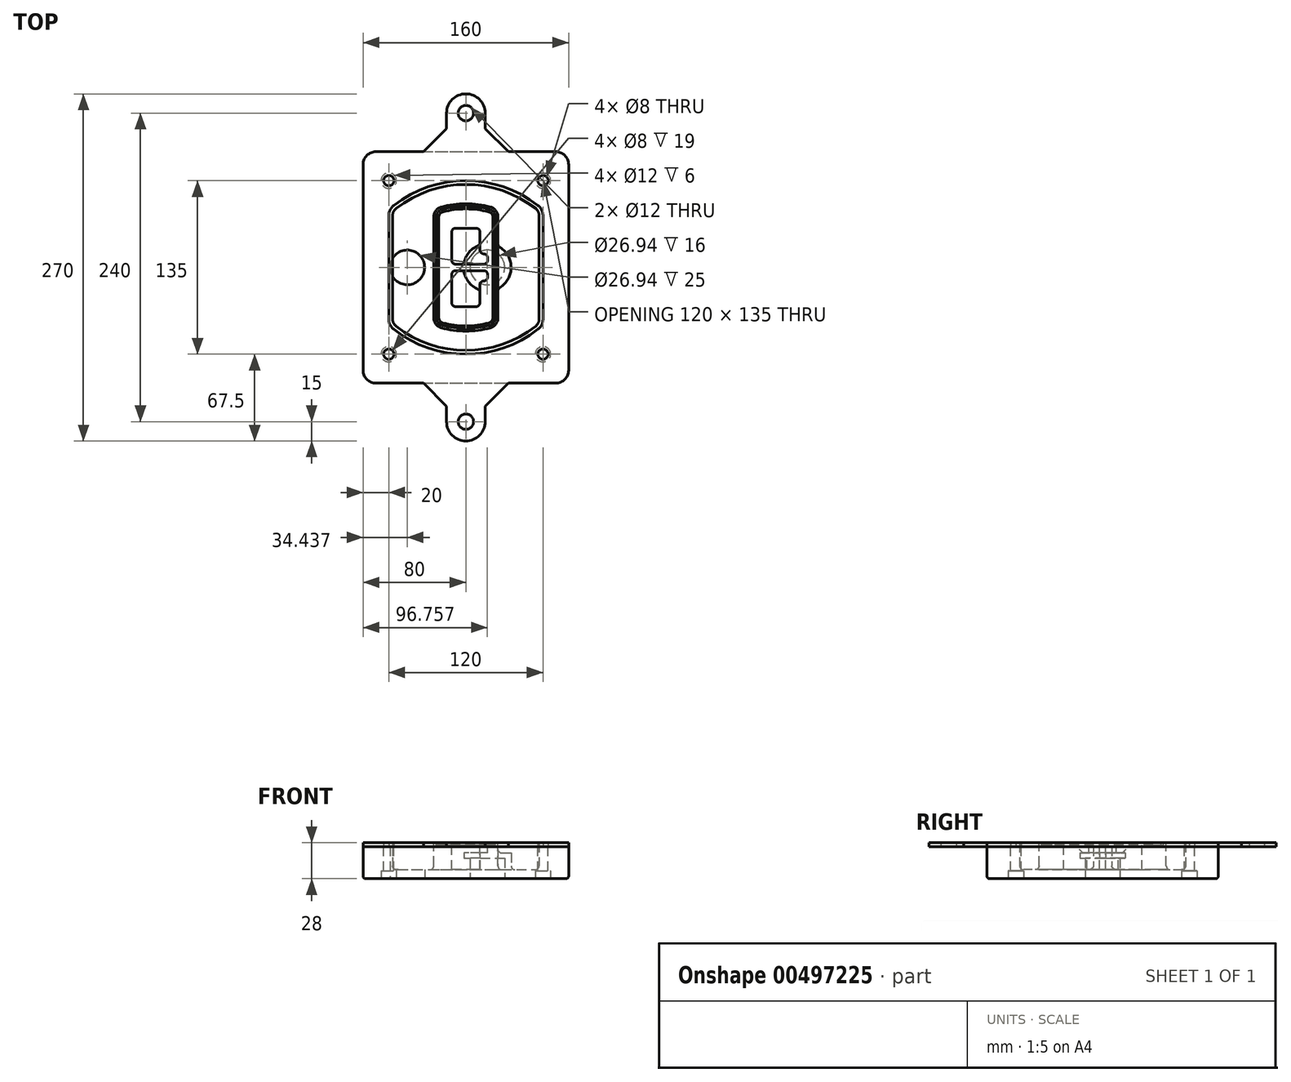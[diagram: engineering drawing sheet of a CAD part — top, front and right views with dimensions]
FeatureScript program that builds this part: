
annotation { "Feature Type Name" : "Feature", "Feature Type Description" : "" }
export const myFeature = defineFeature(function(context is Context, id is Id, definition is map)
    precondition{}
    {
        {
            var Q0;
            Q0=qCreatedBy(makeId("Top.planeOp"),FACE);
            var sketch = newSketch(context, id + "F0", { "sketchPlane" : qUnion([Q0])});
            skPoint(sketch, "E0.rect.middle", {"position": v(0, 0) * mm});
            skLineSegment(sketch, "E1.bottom", {"start": v(-70, -90) * mm, "end": v(70, -90) * mm});
            skLineSegment(sketch, "E1.top", {"start": v(-70, 90) * mm, "end": v(70, 90) * mm});
            skLineSegment(sketch, "E1.left", {"start": v(-80, -80) * mm, "end": v(-80, 80) * mm});
            skLineSegment(sketch, "E1.right", {"start": v(80, -80) * mm, "end": v(80, 80) * mm});
            skLineSegment(sketch, "E2", {"start": v(-80, 90) * mm, "end": v(80, -90) * mm, "construction": true});
            skLineSegment(sketch, "E3", {"start": v(80, 90) * mm, "end": v(-80, -90) * mm, "construction": true});
            skCircle(sketch, "E4", {"center": v(-60, 67.5) * mm, "radius": 4 * mm});
            skCircle(sketch, "E5", {"center": v(60, 67.5) * mm, "radius": 4 * mm});
            skCircle(sketch, "E6", {"center": v(60, -67.5) * mm, "radius": 4 * mm});
            skCircle(sketch, "E7", {"center": v(-60, -67.5) * mm, "radius": 4 * mm});
            skLineSegment(sketch, "E8", {"start": v(-60, 67.5) * mm, "end": v(60, 67.5) * mm, "construction": true});
            skLineSegment(sketch, "E9", {"start": v(60, 67.5) * mm, "end": v(60, -67.5) * mm, "construction": true});
            skLineSegment(sketch, "E10", {"start": v(60, -67.5) * mm, "end": v(-60, -67.5) * mm, "construction": true});
            skLineSegment(sketch, "E11", {"start": v(-60, -67.5) * mm, "end": v(-60, 67.5) * mm, "construction": true});
            skLineSegment(sketch, "E12", {"start": v(-60, 40.3) * mm, "end": v(-60, -40.3) * mm});
            skLineSegment(sketch, "E13", {"start": v(60, 40.3) * mm, "end": v(60, -40.3) * mm});
            skArc(sketch, "E14", {"start": v(56.15, 48.18) * mm, "mid": v(0, 67.5) * mm, "end": v(-56.15, 48.18) * mm});
            skArc(sketch, "E15", {"start": v(-56.15, -48.18) * mm, "mid": v(0, -67.5) * mm, "end": v(56.15, -48.18) * mm});
            skLineSegment(sketch, "E16", {"start": v(-60, 0) * mm, "end": v(60, 0) * mm, "construction": true});
            skPoint(sketch, "E17.visualSharp", {"position": v(-60, -45) * mm});
            skArc(sketch, "E17.filletArc", {"start": v(-60, -40.3) * mm, "mid": v(-58.99, -44.68) * mm, "end": v(-56.15, -48.18) * mm});
            skPoint(sketch, "E18.visualSharp", {"position": v(-60, 45) * mm});
            skArc(sketch, "E18.filletArc", {"start": v(-56.15, 48.18) * mm, "mid": v(-58.99, 44.68) * mm, "end": v(-60, 40.3) * mm});
            skPoint(sketch, "E19.visualSharp", {"position": v(60, 45) * mm});
            skArc(sketch, "E19.filletArc", {"start": v(60, 40.3) * mm, "mid": v(58.99, 44.68) * mm, "end": v(56.15, 48.18) * mm});
            skPoint(sketch, "E20.visualSharp", {"position": v(60, -45) * mm});
            skArc(sketch, "E20.filletArc", {"start": v(56.15, -48.18) * mm, "mid": v(58.99, -44.68) * mm, "end": v(60, -40.3) * mm});
            skPoint(sketch, "E21.visualSharp", {"position": v(-80, 90) * mm});
            skArc(sketch, "E21.filletArc", {"start": v(-70, 90) * mm, "mid": v(-77.07, 87.07) * mm, "end": v(-80, 80) * mm});
            skPoint(sketch, "E22.visualSharp", {"position": v(80, 90) * mm});
            skArc(sketch, "E22.filletArc", {"start": v(80, 80) * mm, "mid": v(77.07, 87.07) * mm, "end": v(70, 90) * mm});
            skPoint(sketch, "E23.visualSharp", {"position": v(80, -90) * mm});
            skArc(sketch, "E23.filletArc", {"start": v(70, -90) * mm, "mid": v(77.07, -87.07) * mm, "end": v(80, -80) * mm});
            skPoint(sketch, "E24.visualSharp", {"position": v(-80, -90) * mm});
            skArc(sketch, "E24.filletArc", {"start": v(-80, -80) * mm, "mid": v(-77.07, -87.07) * mm, "end": v(-70, -90) * mm});
            skArc(sketch, "E25.0", {"start": v(57, 40.3) * mm, "mid": v(56.3, 43.36) * mm, "end": v(54.3, 45.81) * mm});
            skLineSegment(sketch, "E25.1", {"start": v(57, 40.3) * mm, "end": v(57, -40.3) * mm});
            skArc(sketch, "E25.2", {"start": v(54.3, -45.81) * mm, "mid": v(56.3, -43.36) * mm, "end": v(57, -40.3) * mm});
            skArc(sketch, "E25.3", {"start": v(-54.3, -45.81) * mm, "mid": v(0, -64.5) * mm, "end": v(54.3, -45.81) * mm});
            skArc(sketch, "E25.4", {"start": v(-57, -40.3) * mm, "mid": v(-56.3, -43.36) * mm, "end": v(-54.3, -45.81) * mm});
            skArc(sketch, "E25.5", {"start": v(54.3, 45.81) * mm, "mid": v(0, 64.5) * mm, "end": v(-54.3, 45.81) * mm});
            skLineSegment(sketch, "E25.6", {"start": v(-57, 40.3) * mm, "end": v(-57, -40.3) * mm});
            skArc(sketch, "E25.7", {"start": v(-54.3, 45.81) * mm, "mid": v(-56.3, 43.36) * mm, "end": v(-57, 40.3) * mm});
            skArc(sketch, "E26.0", {"start": v(-58.62, 51.33) * mm, "mid": v(-62.58, 46.43) * mm, "end": v(-64, 40.3) * mm});
            skArc(sketch, "E26.1", {"start": v(58.62, 51.33) * mm, "mid": v(0, 71.5) * mm, "end": v(-58.62, 51.33) * mm});
            skArc(sketch, "E26.2", {"start": v(64, 40.3) * mm, "mid": v(62.58, 46.43) * mm, "end": v(58.62, 51.33) * mm});
            skLineSegment(sketch, "E26.3", {"start": v(64, 40.3) * mm, "end": v(64, -40.3) * mm});
            skArc(sketch, "E26.4", {"start": v(58.62, -51.33) * mm, "mid": v(62.58, -46.43) * mm, "end": v(64, -40.3) * mm});
            skLineSegment(sketch, "E26.5", {"start": v(-64, 40.3) * mm, "end": v(-64, -40.3) * mm});
            skArc(sketch, "E26.6", {"start": v(-58.62, -51.33) * mm, "mid": v(0, -71.5) * mm, "end": v(58.62, -51.33) * mm});
            skArc(sketch, "E26.7", {"start": v(-64, -40.3) * mm, "mid": v(-62.58, -46.43) * mm, "end": v(-58.62, -51.33) * mm});
            skSolve(sketch);
        }
        {
            var Q0;
            Q0=makeQuery(id+"F0.imprint","IMPRINT",FACE,{"disambiguationData":[TD([[makeQuery(id+"F0.imprint","IMPRINT",EDGE,{"derivedFrom":sQuery(id+"F0.wireOp",EDGE,"E1.bottom")}),1.0]])]});
            var Q1;
            Q1=makeQuery(id+"F0.imprint","IMPRINT",FACE,{"disambiguationData":[TD([[makeQuery(id+"F0.imprint","IMPRINT",EDGE,{"derivedFrom":sQuery(id+"F0.wireOp",EDGE,"E12")}),1.0]])]});
            var Q2;
            Q2=makeQuery(id+"F0.imprint","IMPRINT",FACE,{"disambiguationData":[TD([[makeQuery(id+"F0.imprint","IMPRINT",EDGE,{"derivedFrom":sQuery(id+"F0.wireOp",EDGE,"E25.0")}),1.0]])]});
            var Q3;
            Q3=makeQuery(id+"F0.imprint","IMPRINT",FACE,{"disambiguationData":[TD([[makeQuery(id+"F0.imprint","IMPRINT",EDGE,{"derivedFrom":sQuery(id+"F0.wireOp",EDGE,"E12")}),-1.0]])]});
            extrude(context, id + "F1", {"entities" : qUnion([Q0, Q1, Q2, Q3]), "oppositeDirection" : true, "depth" : 25 * mm});
        }
        {
            var Q0;
            Q0=makeQuery(id+"F0.imprint","IMPRINT",FACE,{"disambiguationData":[TD([[makeQuery(id+"F0.imprint","IMPRINT",EDGE,{"derivedFrom":sQuery(id+"F0.wireOp",EDGE,"E12")}),1.0]])]});
            extrude(context, id + "F2", {"entities" : qUnion([Q0]), "operationType" : NewBodyOperationType.ADD, "depth" : 3 * mm});
        }
        {
            var Q0;
            Q0=makeQuery(id+"F0.imprint","IMPRINT",FACE,{"disambiguationData":[TD([[makeQuery(id+"F0.imprint","IMPRINT",EDGE,{"derivedFrom":sQuery(id+"F0.wireOp",EDGE,"E25.0")}),1.0]])]});
            extrude(context, id + "F3", {"entities" : qUnion([Q0]), "operationType" : NewBodyOperationType.REMOVE, "oppositeDirection" : true, "depth" : 18 * mm});
        }
        {
            var Q0;
            Q0=makeQuery(id+"F2.opExtrude","CAP_FACE",FACE,{"disambiguationData":[OSD([sQuery(id+"F0.wireOp",EDGE,"E12"),sQuery(id+"F0.wireOp",EDGE,"E13"),sQuery(id+"F0.wireOp",EDGE,"E14"),sQuery(id+"F0.wireOp",EDGE,"E15"),sQuery(id+"F0.wireOp",EDGE,"E17.filletArc"),sQuery(id+"F0.wireOp",EDGE,"E18.filletArc"),sQuery(id+"F0.wireOp",EDGE,"E19.filletArc"),sQuery(id+"F0.wireOp",EDGE,"E20.filletArc"),sQuery(id+"F0.wireOp",EDGE,"E25.0"),sQuery(id+"F0.wireOp",EDGE,"E25.1"),sQuery(id+"F0.wireOp",EDGE,"E25.2"),sQuery(id+"F0.wireOp",EDGE,"E25.3"),sQuery(id+"F0.wireOp",EDGE,"E25.4"),sQuery(id+"F0.wireOp",EDGE,"E25.5"),sQuery(id+"F0.wireOp",EDGE,"E25.6"),sQuery(id+"F0.wireOp",EDGE,"E25.7")])],"isStart":false});
            var sketch = newSketch(context, id + "F4", { "sketchPlane" : qUnion([Q0])});
            skArc(sketch, "E27.0", {"start": v(-19.08, -46.97) * mm, "mid": v(0, -49.5) * mm, "end": v(19.08, -46.97) * mm});
            skArc(sketch, "E28.0", {"start": v(19.08, 46.97) * mm, "mid": v(0, 49.5) * mm, "end": v(-19.08, 46.97) * mm});
            skLineSegment(sketch, "E29", {"start": v(-25, 39.25) * mm, "end": v(-25, -39.25) * mm});
            skLineSegment(sketch, "E30", {"start": v(25, 39.25) * mm, "end": v(25, -39.25) * mm});
            skLineSegment(sketch, "E31", {"start": v(-25, 45.1) * mm, "end": v(25, 45.1) * mm, "construction": true});
            skLineSegment(sketch, "E32", {"start": v(-25, -45.1) * mm, "end": v(25, -45.1) * mm, "construction": true});
            skPoint(sketch, "E33.visualSharp", {"position": v(-25, 45.1) * mm});
            skArc(sketch, "E33.filletArc", {"start": v(-19.08, 46.97) * mm, "mid": v(-23.35, 44.11) * mm, "end": v(-25, 39.25) * mm});
            skPoint(sketch, "E34.visualSharp", {"position": v(25, 45.1) * mm});
            skArc(sketch, "E34.filletArc", {"start": v(25, 39.25) * mm, "mid": v(23.35, 44.11) * mm, "end": v(19.08, 46.97) * mm});
            skPoint(sketch, "E35.visualSharp", {"position": v(25, -45.1) * mm});
            skArc(sketch, "E35.filletArc", {"start": v(19.08, -46.97) * mm, "mid": v(23.35, -44.11) * mm, "end": v(25, -39.25) * mm});
            skPoint(sketch, "E36.visualSharp", {"position": v(-25, -45.1) * mm});
            skArc(sketch, "E36.filletArc", {"start": v(-25, -39.25) * mm, "mid": v(-23.35, -44.11) * mm, "end": v(-19.08, -46.97) * mm});
            skArc(sketch, "E37.0", {"start": v(54.3, 45.81) * mm, "mid": v(0, 64.5) * mm, "end": v(-54.3, 45.81) * mm});
            skArc(sketch, "E37.1", {"start": v(-54.3, 45.81) * mm, "mid": v(-56.3, 43.36) * mm, "end": v(-57, 40.3) * mm});
            skLineSegment(sketch, "E37.2", {"start": v(-57, 40.3) * mm, "end": v(-57, -40.3) * mm});
            skArc(sketch, "E37.3", {"start": v(-57, -40.3) * mm, "mid": v(-56.3, -43.36) * mm, "end": v(-54.3, -45.81) * mm});
            skArc(sketch, "E37.4", {"start": v(-54.3, -45.81) * mm, "mid": v(0, -64.5) * mm, "end": v(54.3, -45.81) * mm});
            skArc(sketch, "E37.5", {"start": v(54.3, -45.81) * mm, "mid": v(56.3, -43.36) * mm, "end": v(57, -40.3) * mm});
            skLineSegment(sketch, "E37.6", {"start": v(57, 40.3) * mm, "end": v(57, -40.3) * mm});
            skArc(sketch, "E37.7", {"start": v(57, 40.3) * mm, "mid": v(56.3, 43.36) * mm, "end": v(54.3, 45.81) * mm});
            skLineSegment(sketch, "E38.0", {"start": v(23, 39.25) * mm, "end": v(23, -39.25) * mm});
            skArc(sketch, "E38.1", {"start": v(18.56, -45.04) * mm, "mid": v(21.76, -42.9) * mm, "end": v(23, -39.25) * mm});
            skArc(sketch, "E38.2", {"start": v(-18.56, -45.04) * mm, "mid": v(0, -47.5) * mm, "end": v(18.56, -45.04) * mm});
            skArc(sketch, "E38.3", {"start": v(-23, -39.25) * mm, "mid": v(-21.76, -42.9) * mm, "end": v(-18.56, -45.04) * mm});
            skLineSegment(sketch, "E38.4", {"start": v(-23, 39.25) * mm, "end": v(-23, -39.25) * mm});
            skArc(sketch, "E38.5", {"start": v(23, 39.25) * mm, "mid": v(21.76, 42.9) * mm, "end": v(18.56, 45.04) * mm});
            skArc(sketch, "E38.6", {"start": v(-18.56, 45.04) * mm, "mid": v(-21.76, 42.9) * mm, "end": v(-23, 39.25) * mm});
            skArc(sketch, "E38.7", {"start": v(18.56, 45.04) * mm, "mid": v(0, 47.5) * mm, "end": v(-18.56, 45.04) * mm});
            skArc(sketch, "E39.0", {"start": v(21, 39.25) * mm, "mid": v(20.18, 41.68) * mm, "end": v(18.04, 43.1) * mm});
            skLineSegment(sketch, "E39.1", {"start": v(21, 39.25) * mm, "end": v(21, -39.25) * mm});
            skArc(sketch, "E39.2", {"start": v(18.04, -43.1) * mm, "mid": v(20.18, -41.68) * mm, "end": v(21, -39.25) * mm});
            skArc(sketch, "E39.3", {"start": v(-18.04, -43.1) * mm, "mid": v(0, -45.5) * mm, "end": v(18.04, -43.1) * mm});
            skArc(sketch, "E39.4", {"start": v(-21, -39.25) * mm, "mid": v(-20.18, -41.68) * mm, "end": v(-18.04, -43.1) * mm});
            skArc(sketch, "E39.5", {"start": v(18.04, 43.1) * mm, "mid": v(0, 45.5) * mm, "end": v(-18.04, 43.1) * mm});
            skLineSegment(sketch, "E39.6", {"start": v(-21, 39.25) * mm, "end": v(-21, -39.25) * mm});
            skArc(sketch, "E39.7", {"start": v(-18.04, 43.1) * mm, "mid": v(-20.18, 41.68) * mm, "end": v(-21, 39.25) * mm});
            skLineSegment(sketch, "E40", {"start": v(-25, 0) * mm, "end": v(25, 0) * mm, "construction": true});
            skLineSegment(sketch, "E41", {"start": v(-11, 5.5) * mm, "end": v(-11, 27.5) * mm});
            skLineSegment(sketch, "E42", {"start": v(-8, 30.5) * mm, "end": v(8, 30.5) * mm});
            skLineSegment(sketch, "E43", {"start": v(11, 27.5) * mm, "end": v(11, 13.5) * mm});
            skLineSegment(sketch, "E44", {"start": v(14, 10.5) * mm, "end": v(14, 10.5) * mm});
            skLineSegment(sketch, "E45", {"start": v(17, 7.5) * mm, "end": v(17, 5.5) * mm});
            skLineSegment(sketch, "E46", {"start": v(14, 2.5) * mm, "end": v(-8, 2.5) * mm});
            skPoint(sketch, "E47.visualSharp", {"position": v(-11, 30.5) * mm});
            skArc(sketch, "E47.filletArc", {"start": v(-8, 30.5) * mm, "mid": v(-10.12, 29.62) * mm, "end": v(-11, 27.5) * mm});
            skPoint(sketch, "E48.visualSharp", {"position": v(11, 30.5) * mm});
            skArc(sketch, "E48.filletArc", {"start": v(11, 27.5) * mm, "mid": v(10.12, 29.62) * mm, "end": v(8, 30.5) * mm});
            skPoint(sketch, "E49.visualSharp", {"position": v(11, 10.5) * mm});
            skArc(sketch, "E49.filletArc", {"start": v(11, 13.5) * mm, "mid": v(11.88, 11.38) * mm, "end": v(14, 10.5) * mm});
            skPoint(sketch, "E50.visualSharp", {"position": v(17, 10.5) * mm});
            skArc(sketch, "E50.filletArc", {"start": v(17, 7.5) * mm, "mid": v(16.12, 9.62) * mm, "end": v(14, 10.5) * mm});
            skPoint(sketch, "E51.visualSharp", {"position": v(17, 2.5) * mm});
            skArc(sketch, "E51.filletArc", {"start": v(14, 2.5) * mm, "mid": v(16.12, 3.38) * mm, "end": v(17, 5.5) * mm});
            skPoint(sketch, "E52.visualSharp", {"position": v(-11, 2.5) * mm});
            skArc(sketch, "E52.filletArc", {"start": v(-11, 5.5) * mm, "mid": v(-10.12, 3.38) * mm, "end": v(-8, 2.5) * mm});
            skLineSegment(sketch, "E53.0.MirrorCS", {"start": v(14, -2.5) * mm, "end": v(-8, -2.5) * mm});
            skArc(sketch, "E54.0.MirrorCS", {"start": v(-11, -5.5) * mm, "mid": v(-10.12, -3.38) * mm, "end": v(-8, -2.5) * mm});
            skLineSegment(sketch, "E55.0.MirrorCS", {"start": v(-11, -5.5) * mm, "end": v(-11, -27.5) * mm});
            skArc(sketch, "E56.0.MirrorCS", {"start": v(-8, -30.5) * mm, "mid": v(-10.12, -29.62) * mm, "end": v(-11, -27.5) * mm});
            skLineSegment(sketch, "E57.0.MirrorCS", {"start": v(-8, -30.5) * mm, "end": v(8, -30.5) * mm});
            skArc(sketch, "E58.0.MirrorCS", {"start": v(11, -27.5) * mm, "mid": v(10.12, -29.62) * mm, "end": v(8, -30.5) * mm});
            skLineSegment(sketch, "E59.0.MirrorCS", {"start": v(11, -27.5) * mm, "end": v(11, -13.5) * mm});
            skArc(sketch, "E60.0.MirrorCS", {"start": v(11, -13.5) * mm, "mid": v(11.88, -11.38) * mm, "end": v(14, -10.5) * mm});
            skArc(sketch, "E61.0.MirrorCS", {"start": v(17, -7.5) * mm, "mid": v(16.12, -9.62) * mm, "end": v(14, -10.5) * mm});
            skLineSegment(sketch, "E62.0.MirrorCS", {"start": v(17, -7.5) * mm, "end": v(17, -5.5) * mm});
            skArc(sketch, "E63.0.MirrorCS", {"start": v(14, -2.5) * mm, "mid": v(16.12, -3.38) * mm, "end": v(17, -5.5) * mm});
            skSolve(sketch);
        }
        {
            var Q0;
            Q0=makeQuery(id+"F4.imprint","IMPRINT",FACE,{"disambiguationData":[TD([[makeQuery(id+"F4.imprint","IMPRINT",EDGE,{"derivedFrom":sQuery(id+"F4.wireOp",EDGE,"E27.0")}),1.0]])]});
            var Q1;
            Q1=makeQuery(id+"F4.imprint","IMPRINT",FACE,{"disambiguationData":[TD([[makeQuery(id+"F4.imprint","IMPRINT",EDGE,{"derivedFrom":sQuery(id+"F4.wireOp",EDGE,"E38.0")}),-1.0]])]});
            var Q2;
            Q2=makeQuery(id+"F4.imprint","IMPRINT",FACE,{"disambiguationData":[TD([[makeQuery(id+"F4.imprint","IMPRINT",EDGE,{"derivedFrom":sQuery(id+"F4.wireOp",EDGE,"E39.0")}),1.0]])]});
            extrude(context, id + "F5", {"entities" : qUnion([Q0, Q1, Q2]), "operationType" : NewBodyOperationType.ADD, "endBound" : BoundingType.UP_TO_NEXT, "oppositeDirection" : true, "depth" : 25 * mm});
        }
        {
            var Q0;
            Q0=makeQuery(id+"F4.imprint","IMPRINT",FACE,{"disambiguationData":[TD([[makeQuery(id+"F4.imprint","IMPRINT",EDGE,{"derivedFrom":sQuery(id+"F4.wireOp",EDGE,"E38.0")}),-1.0]])]});
            extrude(context, id + "F6", {"entities" : qUnion([Q0]), "operationType" : NewBodyOperationType.REMOVE, "oppositeDirection" : true, "depth" : 2 * mm});
        }
        {
            var Q0;
            Q0=makeQuery(id+"F1.opExtrude","CAP_FACE",FACE,{"disambiguationData":[OSD([sQuery(id+"F0.wireOp",EDGE,"E1.bottom"),sQuery(id+"F0.wireOp",EDGE,"E1.top"),sQuery(id+"F0.wireOp",EDGE,"E1.left"),sQuery(id+"F0.wireOp",EDGE,"E1.right"),sQuery(id+"F0.wireOp",EDGE,"E4"),sQuery(id+"F0.wireOp",EDGE,"E5"),sQuery(id+"F0.wireOp",EDGE,"E6"),sQuery(id+"F0.wireOp",EDGE,"E7"),sQuery(id+"F0.wireOp",EDGE,"E21.filletArc"),sQuery(id+"F0.wireOp",EDGE,"E22.filletArc"),sQuery(id+"F0.wireOp",EDGE,"E23.filletArc"),sQuery(id+"F0.wireOp",EDGE,"E24.filletArc")])],"isStart":false});
            var sketch = newSketch(context, id + "F7", { "sketchPlane" : qUnion([Q0])});
            skCircle(sketch, "E64", {"center": v(16.76, 0) * mm, "radius": 13.47 * mm});
            skCircle(sketch, "E65", {"center": v(-45.56, 0) * mm, "radius": 13.47 * mm});
            skLineSegment(sketch, "E66", {"start": v(80, 0) * mm, "end": v(-80, 0) * mm});
            skCircle(sketch, "E67", {"center": v(16.76, 0) * mm, "radius": 18.47 * mm});
            skCircle(sketch, "E68", {"center": v(60, -67.5) * mm, "radius": 6 * mm});
            skCircle(sketch, "E69", {"center": v(-60, -67.5) * mm, "radius": 6 * mm});
            skCircle(sketch, "E70", {"center": v(-60, 67.5) * mm, "radius": 6 * mm});
            skCircle(sketch, "E71", {"center": v(60, 67.5) * mm, "radius": 6 * mm});
            skSolve(sketch);
        }
        {
            var Q0;
            {var subQ1=sQuery(id+"F7.wireOp",EDGE,"E66");var subQ4=sQuery(id+"F7.wireOp",EDGE,"E64");var subQ6=makeQuery(id+"F7.imprint","INTERSECT",VERTEX,{"disambiguationData":[OD(0.0)],"derivedFrom":[subQ4,subQ1]});Q0=makeQuery(id+"F7.imprint","IMPRINT",FACE,{"disambiguationData":[TD([[makeQuery(id+"F7.imprint","IMPRINT",EDGE,{"disambiguationData":[TD([[subQ6,-1.0]])],"derivedFrom":subQ4}),-1.0]])]});}
            var Q1;
            {var subQ0=sQuery(id+"F7.wireOp",EDGE,"E66");var subQ1=sQuery(id+"F7.wireOp",EDGE,"E64");var subQ3=makeQuery(id+"F7.imprint","INTERSECT",VERTEX,{"disambiguationData":[OD(0.0)],"derivedFrom":[subQ1,subQ0]});Q1=makeQuery(id+"F7.imprint","IMPRINT",FACE,{"disambiguationData":[TD([[makeQuery(id+"F7.imprint","IMPRINT",EDGE,{"disambiguationData":[TD([[subQ3,-1.0]])],"derivedFrom":subQ1}),1.0]])]});}
            var Q2;
            {var subQ0=sQuery(id+"F7.wireOp",EDGE,"E66");var subQ1=sQuery(id+"F7.wireOp",EDGE,"E64");var subQ3=makeQuery(id+"F7.imprint","INTERSECT",VERTEX,{"disambiguationData":[OD(0.0)],"derivedFrom":[subQ1,subQ0]});Q2=makeQuery(id+"F7.imprint","IMPRINT",FACE,{"disambiguationData":[TD([[makeQuery(id+"F7.imprint","IMPRINT",EDGE,{"disambiguationData":[TD([[subQ3,1.0]])],"derivedFrom":subQ1}),1.0]])]});}
            var Q3;
            {var subQ1=sQuery(id+"F7.wireOp",EDGE,"E66");var subQ4=sQuery(id+"F7.wireOp",EDGE,"E64");var subQ6=makeQuery(id+"F7.imprint","INTERSECT",VERTEX,{"disambiguationData":[OD(0.0)],"derivedFrom":[subQ4,subQ1]});Q3=makeQuery(id+"F7.imprint","IMPRINT",FACE,{"disambiguationData":[TD([[makeQuery(id+"F7.imprint","IMPRINT",EDGE,{"disambiguationData":[TD([[subQ6,1.0]])],"derivedFrom":subQ4}),-1.0]])]});}
            extrude(context, id + "F8", {"entities" : qUnion([Q0, Q1, Q2, Q3]), "operationType" : NewBodyOperationType.ADD, "oppositeDirection" : true, "depth" : 20 * mm});
        }
        {
            var Q0;
            {var subQ0=sQuery(id+"F7.wireOp",EDGE,"E66");var subQ1=sQuery(id+"F7.wireOp",EDGE,"E64");var subQ3=makeQuery(id+"F7.imprint","INTERSECT",VERTEX,{"disambiguationData":[OD(0.0)],"derivedFrom":[subQ1,subQ0]});Q0=makeQuery(id+"F7.imprint","IMPRINT",FACE,{"disambiguationData":[TD([[makeQuery(id+"F7.imprint","IMPRINT",EDGE,{"disambiguationData":[TD([[subQ3,-1.0]])],"derivedFrom":subQ1}),1.0]])]});}
            var Q1;
            {var subQ0=sQuery(id+"F7.wireOp",EDGE,"E66");var subQ1=sQuery(id+"F7.wireOp",EDGE,"E64");var subQ3=makeQuery(id+"F7.imprint","INTERSECT",VERTEX,{"disambiguationData":[OD(0.0)],"derivedFrom":[subQ1,subQ0]});Q1=makeQuery(id+"F7.imprint","IMPRINT",FACE,{"disambiguationData":[TD([[makeQuery(id+"F7.imprint","IMPRINT",EDGE,{"disambiguationData":[TD([[subQ3,1.0]])],"derivedFrom":subQ1}),1.0]])]});}
            extrude(context, id + "F9", {"entities" : qUnion([Q0, Q1]), "operationType" : NewBodyOperationType.REMOVE, "oppositeDirection" : true, "depth" : 16 * mm});
        }
        {
            var Q0;
            {var subQ0=sQuery(id+"F7.wireOp",EDGE,"E66");var subQ1=sQuery(id+"F7.wireOp",EDGE,"E65");var subQ3=makeQuery(id+"F7.imprint","INTERSECT",VERTEX,{"disambiguationData":[OD(0.0)],"derivedFrom":[subQ1,subQ0]});Q0=makeQuery(id+"F7.imprint","IMPRINT",FACE,{"disambiguationData":[TD([[makeQuery(id+"F7.imprint","IMPRINT",EDGE,{"disambiguationData":[TD([[subQ3,-1.0]])],"derivedFrom":subQ1}),1.0]])]});}
            var Q1;
            {var subQ0=sQuery(id+"F7.wireOp",EDGE,"E66");var subQ1=sQuery(id+"F7.wireOp",EDGE,"E65");var subQ3=makeQuery(id+"F7.imprint","INTERSECT",VERTEX,{"disambiguationData":[OD(0.0)],"derivedFrom":[subQ1,subQ0]});Q1=makeQuery(id+"F7.imprint","IMPRINT",FACE,{"disambiguationData":[TD([[makeQuery(id+"F7.imprint","IMPRINT",EDGE,{"disambiguationData":[TD([[subQ3,1.0]])],"derivedFrom":subQ1}),1.0]])]});}
            extrude(context, id + "F10", {"entities" : qUnion([Q0, Q1]), "operationType" : NewBodyOperationType.REMOVE, "oppositeDirection" : true, "depth" : 25 * mm});
        }
        {
            var Q0;
            Q0=makeQuery(id+"F7.imprint","IMPRINT",FACE,{"disambiguationData":[TD([[makeQuery(id+"F7.imprint","IMPRINT",EDGE,{"derivedFrom":sQuery(id+"F7.wireOp",EDGE,"E68")}),1.0]])]});
            var Q1;
            Q1=makeQuery(id+"F7.imprint","IMPRINT",FACE,{"disambiguationData":[TD([[makeQuery(id+"F7.imprint","IMPRINT",EDGE,{"derivedFrom":makeQuery(id+"F1.opExtrude","CAP_EDGE",EDGE,{"disambiguationData":[OSD([sQuery(id+"F0.wireOp",EDGE,"E5")])],"isStart":false})}),-1.0]])]});
            var Q2;
            Q2=makeQuery(id+"F7.imprint","IMPRINT",FACE,{"disambiguationData":[TD([[makeQuery(id+"F7.imprint","IMPRINT",EDGE,{"derivedFrom":sQuery(id+"F7.wireOp",EDGE,"E69")}),1.0]])]});
            var Q3;
            Q3=makeQuery(id+"F7.imprint","IMPRINT",FACE,{"disambiguationData":[TD([[makeQuery(id+"F7.imprint","IMPRINT",EDGE,{"derivedFrom":makeQuery(id+"F1.opExtrude","CAP_EDGE",EDGE,{"disambiguationData":[OSD([sQuery(id+"F0.wireOp",EDGE,"E4")])],"isStart":false})}),-1.0]])]});
            var Q4;
            Q4=makeQuery(id+"F7.imprint","IMPRINT",FACE,{"disambiguationData":[TD([[makeQuery(id+"F7.imprint","IMPRINT",EDGE,{"derivedFrom":sQuery(id+"F7.wireOp",EDGE,"E70")}),1.0]])]});
            var Q5;
            Q5=makeQuery(id+"F7.imprint","IMPRINT",FACE,{"disambiguationData":[TD([[makeQuery(id+"F7.imprint","IMPRINT",EDGE,{"derivedFrom":makeQuery(id+"F1.opExtrude","CAP_EDGE",EDGE,{"disambiguationData":[OSD([sQuery(id+"F0.wireOp",EDGE,"E7")])],"isStart":false})}),-1.0]])]});
            var Q6;
            Q6=makeQuery(id+"F7.imprint","IMPRINT",FACE,{"disambiguationData":[TD([[makeQuery(id+"F7.imprint","IMPRINT",EDGE,{"derivedFrom":sQuery(id+"F7.wireOp",EDGE,"E71")}),1.0]])]});
            var Q7;
            Q7=makeQuery(id+"F7.imprint","IMPRINT",FACE,{"disambiguationData":[TD([[makeQuery(id+"F7.imprint","IMPRINT",EDGE,{"derivedFrom":makeQuery(id+"F1.opExtrude","CAP_EDGE",EDGE,{"disambiguationData":[OSD([sQuery(id+"F0.wireOp",EDGE,"E6")])],"isStart":false})}),-1.0]])]});
            extrude(context, id + "F11", {"entities" : qUnion([Q0, Q1, Q2, Q3, Q4, Q5, Q6, Q7]), "operationType" : NewBodyOperationType.REMOVE, "oppositeDirection" : true, "depth" : 6 * mm});
        }
        {
            var Q0;
            Q0=makeQuery(id+"F9.boolean.opBoolean","COPY",FACE,{"derivedFrom":makeQuery(id+"F9.opExtrude","CAP_FACE",FACE,{"disambiguationData":[OSD([sQuery(id+"F7.wireOp",EDGE,"E64")])],"isStart":false})});
            var sketch = newSketch(context, id + "F12", { "sketchPlane" : qUnion([Q0])});
            skArc(sketch, "E72.0", {"start": v(11, 17.55) * mm, "mid": v(2.57, 11.82) * mm, "end": v(-1.54, 2.5) * mm});
            skArc(sketch, "E72.1", {"start": v(-1.54, -2.5) * mm, "mid": v(2.57, -11.82) * mm, "end": v(11, -17.55) * mm});
            skLineSegment(sketch, "E73", {"start": v(-1.54, -2.5) * mm, "end": v(14, -2.5) * mm});
            skLineSegment(sketch, "E74.0", {"start": v(14, 2.5) * mm, "end": v(-1.54, 2.5) * mm});
            skArc(sketch, "E74.1", {"start": v(14, 2.5) * mm, "mid": v(16.12, 3.38) * mm, "end": v(17, 5.5) * mm});
            skLineSegment(sketch, "E74.2", {"start": v(17, 7.5) * mm, "end": v(17, 5.5) * mm});
            skArc(sketch, "E74.3", {"start": v(17, 7.5) * mm, "mid": v(16.12, 9.62) * mm, "end": v(14, 10.5) * mm});
            skArc(sketch, "E74.4", {"start": v(11, 13.5) * mm, "mid": v(11.88, 11.38) * mm, "end": v(14, 10.5) * mm});
            skLineSegment(sketch, "E74.5", {"start": v(11, 17.55) * mm, "end": v(11, 13.5) * mm});
            skLineSegment(sketch, "E74.7", {"start": v(14, -2.5) * mm, "end": v(-1.54, -2.5) * mm});
            skArc(sketch, "E74.8", {"start": v(14, -2.5) * mm, "mid": v(16.12, -3.38) * mm, "end": v(17, -5.5) * mm});
            skLineSegment(sketch, "E74.9", {"start": v(17, -7.5) * mm, "end": v(17, -5.5) * mm});
            skArc(sketch, "E74.10", {"start": v(17, -7.5) * mm, "mid": v(16.12, -9.62) * mm, "end": v(14, -10.5) * mm});
            skArc(sketch, "E74.11", {"start": v(11, -13.5) * mm, "mid": v(11.88, -11.38) * mm, "end": v(14, -10.5) * mm});
            skLineSegment(sketch, "E74.12", {"start": v(11, -17.55) * mm, "end": v(11, -13.5) * mm});
            skPoint(sketch, "E75.orphan", {"position": v(11, -27.5) * mm});
            skPoint(sketch, "E76.orphan", {"position": v(-8, -2.5) * mm});
            skPoint(sketch, "E77.orphan", {"position": v(-8, 2.5) * mm});
            skPoint(sketch, "E78.orphan", {"position": v(11, 27.5) * mm});
            skSolve(sketch);
        }
        {
            var Q0;
            {var subQ7=sQuery(id+"F12.wireOp",EDGE,"E72.0");var subQ14=sQuery(id+"F12.wireOp",EDGE,"E72.1");var subQ16=sQuery(id+"F12.wireOp",EDGE,"E74.1");var subQ18=sQuery(id+"F12.wireOp",EDGE,"E74.8");Q0=qUnion([makeQuery(id+"F12.imprint","IMPRINT",FACE,{"disambiguationData":[TD([[makeQuery(id+"F12.imprint","IMPRINT",EDGE,{"derivedFrom":subQ7}),1.0]])]}),makeQuery(id+"F12.imprint","IMPRINT",FACE,{"disambiguationData":[TD([[makeQuery(id+"F12.imprint","IMPRINT",EDGE,{"derivedFrom":subQ14}),1.0]])]}),makeQuery(id+"F12.imprint","IMPRINT",FACE,{"disambiguationData":[TD([[makeQuery(id+"F12.imprint","IMPRINT",EDGE,{"derivedFrom":subQ16}),1.0]])]}),makeQuery(id+"F12.imprint","IMPRINT",FACE,{"disambiguationData":[TD([[makeQuery(id+"F12.imprint","IMPRINT",EDGE,{"derivedFrom":subQ18}),-1.0]])]})]);}
            var Q1;
            Q1=makeQuery(id+"F5.boolean.opBoolean","SPLIT",FACE,{"disambiguationData":[TD([makeQuery(id+"F5.opExtrude","SWEPT_FACE",FACE,{"disambiguationData":[OSD([sQuery(id+"F4.wireOp",EDGE,"E41")])]})])],"derivedFrom":makeQuery(id+"F3.boolean.opBoolean","COPY",FACE,{"derivedFrom":makeQuery(id+"F3.opExtrude","CAP_FACE",FACE,{"disambiguationData":[OSD([sQuery(id+"F0.wireOp",EDGE,"E25.0"),sQuery(id+"F0.wireOp",EDGE,"E25.1"),sQuery(id+"F0.wireOp",EDGE,"E25.2"),sQuery(id+"F0.wireOp",EDGE,"E25.3"),sQuery(id+"F0.wireOp",EDGE,"E25.4"),sQuery(id+"F0.wireOp",EDGE,"E25.5"),sQuery(id+"F0.wireOp",EDGE,"E25.6"),sQuery(id+"F0.wireOp",EDGE,"E25.7")])],"isStart":false})})});
            extrude(context, id + "F13", {"entities" : qUnion([Q0]), "operationType" : NewBodyOperationType.REMOVE, "endBound" : BoundingType.UP_TO_SURFACE, "endBoundEntityFace" : qUnion([Q1]), "depth" : 25 * mm});
        }
        {
            var Q0;
            Q0=makeQuery(id+"F3.boolean.opBoolean","COPY",EDGE,{"derivedFrom":makeQuery(id+"F3.opExtrude","CAP_EDGE",EDGE,{"disambiguationData":[OSD([sQuery(id+"F0.wireOp",EDGE,"E25.6")])],"isStart":false})});
            var Q1;
            Q1=makeQuery(id+"F8.boolean.opBoolean","INTERSECT",EDGE,{"derivedFrom":[makeQuery(id+"F5.opExtrude","SWEPT_FACE",FACE,{"disambiguationData":[OSD([sQuery(id+"F4.wireOp",EDGE,"E30")])]}),makeQuery(id+"F8.opExtrude","CAP_FACE",FACE,{"disambiguationData":[OSD([sQuery(id+"F7.wireOp",EDGE,"E67")])],"isStart":false})]});
            var Q2;
            Q2=makeQuery(id+"F8.boolean.opBoolean","INTERSECT",EDGE,{"disambiguationData":[OD(1.0)],"derivedFrom":[makeQuery(id+"F5.opExtrude","SWEPT_FACE",FACE,{"disambiguationData":[OSD([sQuery(id+"F4.wireOp",EDGE,"E30")])]}),makeQuery(id+"F8.opExtrude","SWEPT_FACE",FACE,{"disambiguationData":[OSD([sQuery(id+"F7.wireOp",EDGE,"E67")])]})]});
            var Q3;
            {var subQ0=sQuery(id+"F4.wireOp",EDGE,"E30");Q3=makeQuery(id+"F8.boolean.opBoolean","SPLIT",EDGE,{"disambiguationData":[TD([makeQuery(id+"F5.opExtrude","SWEPT_FACE",FACE,{"disambiguationData":[OSD([sQuery(id+"F4.wireOp",EDGE,"E35.filletArc")])]})])],"derivedFrom":makeQuery(id+"F5.opExtrude","CAP_EDGE",EDGE,{"disambiguationData":[OSD([subQ0])],"isStart":false})});}
            var Q4;
            {var subQ0=sQuery(id+"F0.wireOp",EDGE,"E25.7");var subQ1=sQuery(id+"F0.wireOp",EDGE,"E25.1");var subQ2=sQuery(id+"F0.wireOp",EDGE,"E25.6");var subQ3=sQuery(id+"F0.wireOp",EDGE,"E25.5");var subQ4=sQuery(id+"F0.wireOp",EDGE,"E25.4");var subQ5=sQuery(id+"F0.wireOp",EDGE,"E25.0");var subQ6=sQuery(id+"F0.wireOp",EDGE,"E25.2");var subQ7=sQuery(id+"F0.wireOp",EDGE,"E25.3");Q4=makeQuery(id+"F8.boolean.opBoolean","INTERSECT",EDGE,{"derivedFrom":[makeQuery(id+"F5.boolean.opBoolean","SPLIT",FACE,{"disambiguationData":[TD([makeQuery(id+"F2.opExtrude","SWEPT_FACE",FACE,{"disambiguationData":[OSD([subQ5])]})])],"derivedFrom":makeQuery(id+"F3.boolean.opBoolean","COPY",FACE,{"derivedFrom":makeQuery(id+"F3.opExtrude","CAP_FACE",FACE,{"disambiguationData":[OSD([subQ5,subQ1,subQ6,subQ7,subQ4,subQ3,subQ2,subQ0])],"isStart":false})})}),makeQuery(id+"F8.opExtrude","SWEPT_FACE",FACE,{"disambiguationData":[OSD([sQuery(id+"F7.wireOp",EDGE,"E67")])]})]});}
            var Q5;
            Q5=makeQuery(id+"F8.boolean.opBoolean","INTERSECT",EDGE,{"disambiguationData":[OD(0.0)],"derivedFrom":[makeQuery(id+"F5.opExtrude","SWEPT_FACE",FACE,{"disambiguationData":[OSD([sQuery(id+"F4.wireOp",EDGE,"E30")])]}),makeQuery(id+"F8.opExtrude","SWEPT_FACE",FACE,{"disambiguationData":[OSD([sQuery(id+"F7.wireOp",EDGE,"E67")])]})]});
            fillet(context, id + "F14", {"entities" : qUnion([Q0, Q1, Q2, Q3, Q4, Q5]), "radius" : 3 * mm, "tangentPropagation" : true, "allowEdgeOverflow" : false});
        }
        {
            var Q0;
            Q0=makeQuery(id+"F1.opExtrude","CAP_EDGE",EDGE,{"disambiguationData":[OSD([sQuery(id+"F0.wireOp",EDGE,"E1.bottom")])],"isStart":false});
            fillet(context, id + "F15", {"entities" : qUnion([Q0]), "radius" : 2 * mm, "tangentPropagation" : true, "allowEdgeOverflow" : false});
        }
        {
            var Q0;
            {var subQ0=sQuery(id+"F0.wireOp",EDGE,"E21.filletArc");var subQ1=sQuery(id+"F0.wireOp",EDGE,"E7");var subQ2=sQuery(id+"F0.wireOp",EDGE,"E6");var subQ3=sQuery(id+"F0.wireOp",EDGE,"E5");var subQ4=sQuery(id+"F0.wireOp",EDGE,"E4");var subQ5=sQuery(id+"F0.wireOp",EDGE,"E22.filletArc");var subQ6=sQuery(id+"F0.wireOp",EDGE,"E1.bottom");var subQ7=sQuery(id+"F0.wireOp",EDGE,"E1.right");var subQ8=sQuery(id+"F0.wireOp",EDGE,"E1.top");var subQ9=sQuery(id+"F0.wireOp",EDGE,"E1.left");var subQ10=sQuery(id+"F0.wireOp",EDGE,"E23.filletArc");var subQ11=sQuery(id+"F0.wireOp",EDGE,"E24.filletArc");Q0=makeQuery(id+"F2.boolean.opBoolean","SPLIT",FACE,{"disambiguationData":[TD([makeQuery(id+"F1.opExtrude","SWEPT_FACE",FACE,{"disambiguationData":[OSD([subQ6])]})])],"derivedFrom":makeQuery(id+"F1.opExtrude","CAP_FACE",FACE,{"disambiguationData":[OSD([subQ6,subQ8,subQ9,subQ7,subQ4,subQ3,subQ2,subQ1,subQ0,subQ5,subQ10,subQ11])],"isStart":true})});}
            var sketch = newSketch(context, id + "F16", { "sketchPlane" : qUnion([Q0])});
            skLineSegment(sketch, "E79", {"start": v(0, 90) * mm, "end": v(0, 120) * mm, "construction": true});
            skCircle(sketch, "E80", {"center": v(0, 120) * mm, "radius": 6 * mm});
            skLineSegment(sketch, "E81", {"start": v(-33, 90) * mm, "end": v(-15, 108) * mm});
            skLineSegment(sketch, "E82", {"start": v(-15, 108) * mm, "end": v(-15, 120) * mm});
            skLineSegment(sketch, "E83", {"start": v(33, 90) * mm, "end": v(15, 108) * mm});
            skLineSegment(sketch, "E84", {"start": v(15, 108) * mm, "end": v(15, 120) * mm});
            skArc(sketch, "E85", {"start": v(15, 120) * mm, "mid": v(0, 135) * mm, "end": v(-15, 120) * mm});
            skLineSegment(sketch, "E86", {"start": v(-80, 0) * mm, "end": v(80, 0) * mm, "construction": true});
            skLineSegment(sketch, "E87.MirrorCS", {"start": v(0, -90) * mm, "end": v(0, -120) * mm, "construction": true});
            skCircle(sketch, "E88.MirrorC", {"center": v(0, -120) * mm, "radius": 6 * mm});
            skLineSegment(sketch, "E89.MirrorCS", {"start": v(15, -108) * mm, "end": v(15, -120) * mm});
            skLineSegment(sketch, "E90.MirrorCS", {"start": v(33, -90) * mm, "end": v(15, -108) * mm});
            skLineSegment(sketch, "E91.MirrorCS", {"start": v(-15, -108) * mm, "end": v(-15, -120) * mm});
            skLineSegment(sketch, "E92.MirrorCS", {"start": v(-33, -90) * mm, "end": v(-15, -108) * mm});
            skArc(sketch, "E93.MirrorCS", {"start": v(15, -120) * mm, "mid": v(0, -135) * mm, "end": v(-15, -120) * mm});
            skSolve(sketch);
        }
        {
            var Q0;
            Q0=makeQuery(id+"F16.imprint","IMPRINT",FACE,{"disambiguationData":[TD([[makeQuery(id+"F16.imprint","IMPRINT",EDGE,{"derivedFrom":sQuery(id+"F16.wireOp",EDGE,"E80")}),-1.0]])]});
            var Q1;
            Q1=makeQuery(id+"F16.imprint","IMPRINT",FACE,{"disambiguationData":[TD([[makeQuery(id+"F16.imprint","IMPRINT",EDGE,{"derivedFrom":makeQuery(id+"F1.opExtrude","CAP_EDGE",EDGE,{"disambiguationData":[OSD([sQuery(id+"F0.wireOp",EDGE,"E1.left")])],"isStart":true})}),-1.0]])]});
            var Q2;
            Q2=makeQuery(id+"F16.imprint","IMPRINT",FACE,{"disambiguationData":[TD([[makeQuery(id+"F16.imprint","IMPRINT",EDGE,{"derivedFrom":sQuery(id+"F16.wireOp",EDGE,"E89.MirrorCS")}),-1.0]])]});
            var Q3;
            Q3=makeQuery(id+"F2.opExtrude","CAP_FACE",FACE,{"disambiguationData":[OSD([sQuery(id+"F0.wireOp",EDGE,"E12"),sQuery(id+"F0.wireOp",EDGE,"E13"),sQuery(id+"F0.wireOp",EDGE,"E14"),sQuery(id+"F0.wireOp",EDGE,"E15"),sQuery(id+"F0.wireOp",EDGE,"E17.filletArc"),sQuery(id+"F0.wireOp",EDGE,"E18.filletArc"),sQuery(id+"F0.wireOp",EDGE,"E19.filletArc"),sQuery(id+"F0.wireOp",EDGE,"E20.filletArc"),sQuery(id+"F0.wireOp",EDGE,"E25.0"),sQuery(id+"F0.wireOp",EDGE,"E25.1"),sQuery(id+"F0.wireOp",EDGE,"E25.2"),sQuery(id+"F0.wireOp",EDGE,"E25.3"),sQuery(id+"F0.wireOp",EDGE,"E25.4"),sQuery(id+"F0.wireOp",EDGE,"E25.5"),sQuery(id+"F0.wireOp",EDGE,"E25.6"),sQuery(id+"F0.wireOp",EDGE,"E25.7")])],"isStart":false});
            extrude(context, id + "F17", {"entities" : qUnion([Q0, Q1, Q2]), "endBound" : BoundingType.UP_TO_SURFACE, "endBoundEntityFace" : qUnion([Q3]), "depth" : 25 * mm});
        }
    });
